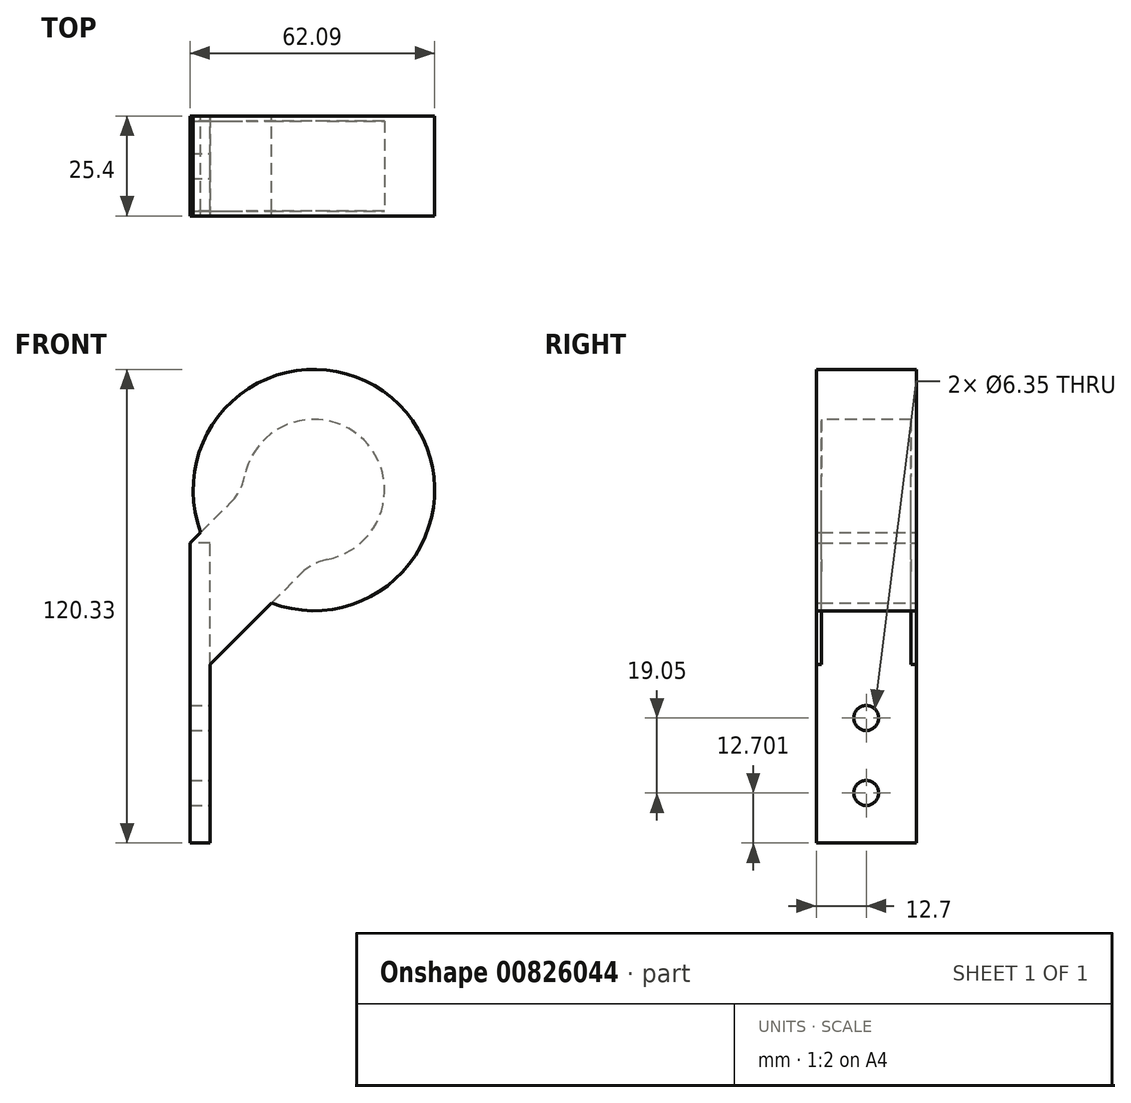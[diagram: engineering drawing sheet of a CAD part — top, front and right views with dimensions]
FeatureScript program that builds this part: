
annotation { "Feature Type Name" : "Feature", "Feature Type Description" : "" }
export const myFeature = defineFeature(function(context is Context, id is Id, definition is map)
    precondition{}
    {
        {
            var Q0;
            Q0=qCreatedBy(makeId("Front.planeOp"),FACE);
            var sketch = newSketch(context, id + "F0", { "sketchPlane" : qUnion([Q0])});
            skLineSegment(sketch, "E0", {"start": v(-98.62, 0) * mm, "end": v(108.18, 0) * mm, "construction": true});
            skLineSegment(sketch, "E1", {"start": v(0, 87.63) * mm, "end": v(0, -82.73) * mm, "construction": true});
            skLineSegment(sketch, "E2", {"start": v(0, 0) * mm, "end": v(31.43, 31.43) * mm, "construction": true});
            skLineSegment(sketch, "E3.0", {"start": v(0, -17.96) * mm, "end": v(28.27, 10.3) * mm});
            skLineSegment(sketch, "E4.0", {"start": v(0, 17.96) * mm, "end": v(10.3, 28.27) * mm});
            skLineSegment(sketch, "E5", {"start": v(31.43, 31.43) * mm, "end": v(-16.41, 31.43) * mm, "construction": true});
            skLineSegment(sketch, "E6", {"start": v(31.43, 31.43) * mm, "end": v(31.43, -18.46) * mm, "construction": true});
            skArc(sketch, "E7", {"start": v(13.8, 34.84) * mm, "mid": v(44.13, 44.13) * mm, "end": v(34.84, 13.8) * mm});
            skPoint(sketch, "E8.visualSharp", {"position": v(13.47, 31.43) * mm});
            skArc(sketch, "E8.filletArc", {"start": v(10.3, 28.27) * mm, "mid": v(12.54, 31.3) * mm, "end": v(13.8, 34.84) * mm});
            skPoint(sketch, "E9.visualSharp", {"position": v(31.43, 13.47) * mm});
            skArc(sketch, "E9.filletArc", {"start": v(34.84, 13.8) * mm, "mid": v(31.3, 12.54) * mm, "end": v(28.27, 10.3) * mm});
            skArc(sketch, "E10.0", {"start": v(2.72, 20.68) * mm, "mid": v(53.11, 53.11) * mm, "end": v(20.68, 2.72) * mm});
            skLineSegment(sketch, "E11", {"start": v(0, 17.96) * mm, "end": v(0, -17.96) * mm});
            skSolve(sketch);
        }
        {
            var Q0;
            Q0=makeQuery(id+"F0.imprint","IMPRINT",FACE,{"disambiguationData":[TD([[makeQuery(id+"F0.imprint","IMPRINT",EDGE,{"derivedFrom":sQuery(id+"F0.wireOp",EDGE,"E7")}),-1.0]])]});
            var Q1;
            Q1=makeQuery(id+"F0.imprint","IMPRINT",FACE,{"disambiguationData":[TD([[makeQuery(id+"F0.imprint","IMPRINT",EDGE,{"derivedFrom":sQuery(id+"F0.wireOp",EDGE,"E7")}),1.0]])]});
            extrude(context, id + "F1", {"entities" : qUnion([Q0, Q1]), "depth" : 12.7 * mm, "offsetDistance" : 25.4 * mm, "hasSecondDirection" : true, "secondDirectionOppositeDirection" : true, "secondDirectionDepth" : 12.7 * mm});
        }
        {
            var Q0;
            Q0=makeQuery(id+"F0.imprint","IMPRINT",FACE,{"disambiguationData":[TD([[makeQuery(id+"F0.imprint","IMPRINT",EDGE,{"derivedFrom":sQuery(id+"F0.wireOp",EDGE,"E7")}),1.0]])]});
            extrude(context, id + "F2", {"entities" : qUnion([Q0]), "operationType" : NewBodyOperationType.REMOVE, "oppositeDirection" : true, "depth" : 11.43 * mm, "offsetDistance" : 25.4 * mm, "hasSecondDirection" : true, "secondDirectionOppositeDirection" : false, "secondDirectionDepth" : 11.43 * mm});
        }
        {
            var Q0;
            Q0=qCreatedBy(makeId("Right.planeOp"),FACE);
            var sketch = newSketch(context, id + "F3", { "sketchPlane" : qUnion([Q0])});
            skLineSegment(sketch, "E12", {"start": v(12.7, 17.96) * mm, "end": v(12.7, -58.24) * mm});
            skLineSegment(sketch, "E13", {"start": v(-12.7, 17.96) * mm, "end": v(12.7, 17.96) * mm});
            skLineSegment(sketch, "E14", {"start": v(-12.7, 17.96) * mm, "end": v(-12.7, -58.24) * mm});
            skLineSegment(sketch, "E15", {"start": v(12.7, -58.24) * mm, "end": v(-12.7, -58.24) * mm});
            skSolve(sketch);
        }
        {
            var Q0;
            Q0 = qSketchRegion(id + "F3", true);
            extrude(context, id + "F4", {"entities" : qUnion([Q0]), "operationType" : NewBodyOperationType.ADD, "depth" : 5.08 * mm, "offsetDistance" : 25.4 * mm});
        }
        {
            var Q0;
            Q0=makeQuery(id+"F4.opExtrude","CAP_FACE",FACE,{"disambiguationData":[OSD([sQuery(id+"F3.wireOp",EDGE,"E12"),sQuery(id+"F3.wireOp",EDGE,"E13"),sQuery(id+"F3.wireOp",EDGE,"E14"),sQuery(id+"F3.wireOp",EDGE,"E15")])],"isStart":false});
            var sketch = newSketch(context, id + "F5", { "sketchPlane" : qUnion([Q0])});
            skPoint(sketch, "E16", {"position": v(0, -26.49) * mm});
            skPoint(sketch, "E17", {"position": v(0, -45.54) * mm});
            skSolve(sketch);
        }
        {
            var Q0;
            Q0=sQuery(id+"F5.wireOp",VERTEX,"E16");
            var Q1;
            Q1=sQuery(id+"F5.wireOp",VERTEX,"E17");
            var Q2;
            Q2=makeQuery(id+"F1.opExtrude","SWEPT_BODY",BODY,{"disambiguationData":[OSD([sQuery(id+"F0.wireOp",EDGE,"E3.0"),sQuery(id+"F0.wireOp",EDGE,"E4.0"),sQuery(id+"F0.wireOp",EDGE,"E10.0"),sQuery(id+"F0.wireOp",EDGE,"E11")])]});
            hole(context, id + "F6", {"style" : HoleStyle.SIMPLE, "endStyle" : HoleEndStyle.THROUGH, "holeDiameter" : 6.35 * mm, "majorDiameter" : 6.35 * mm, "isTappedThrough" : true, "tappedDepth" : 12.7 * mm, "tapClearance" : 3, "locations" : qUnion([Q0, Q1]), "scope" : qUnion([Q2])});
        }
    });
